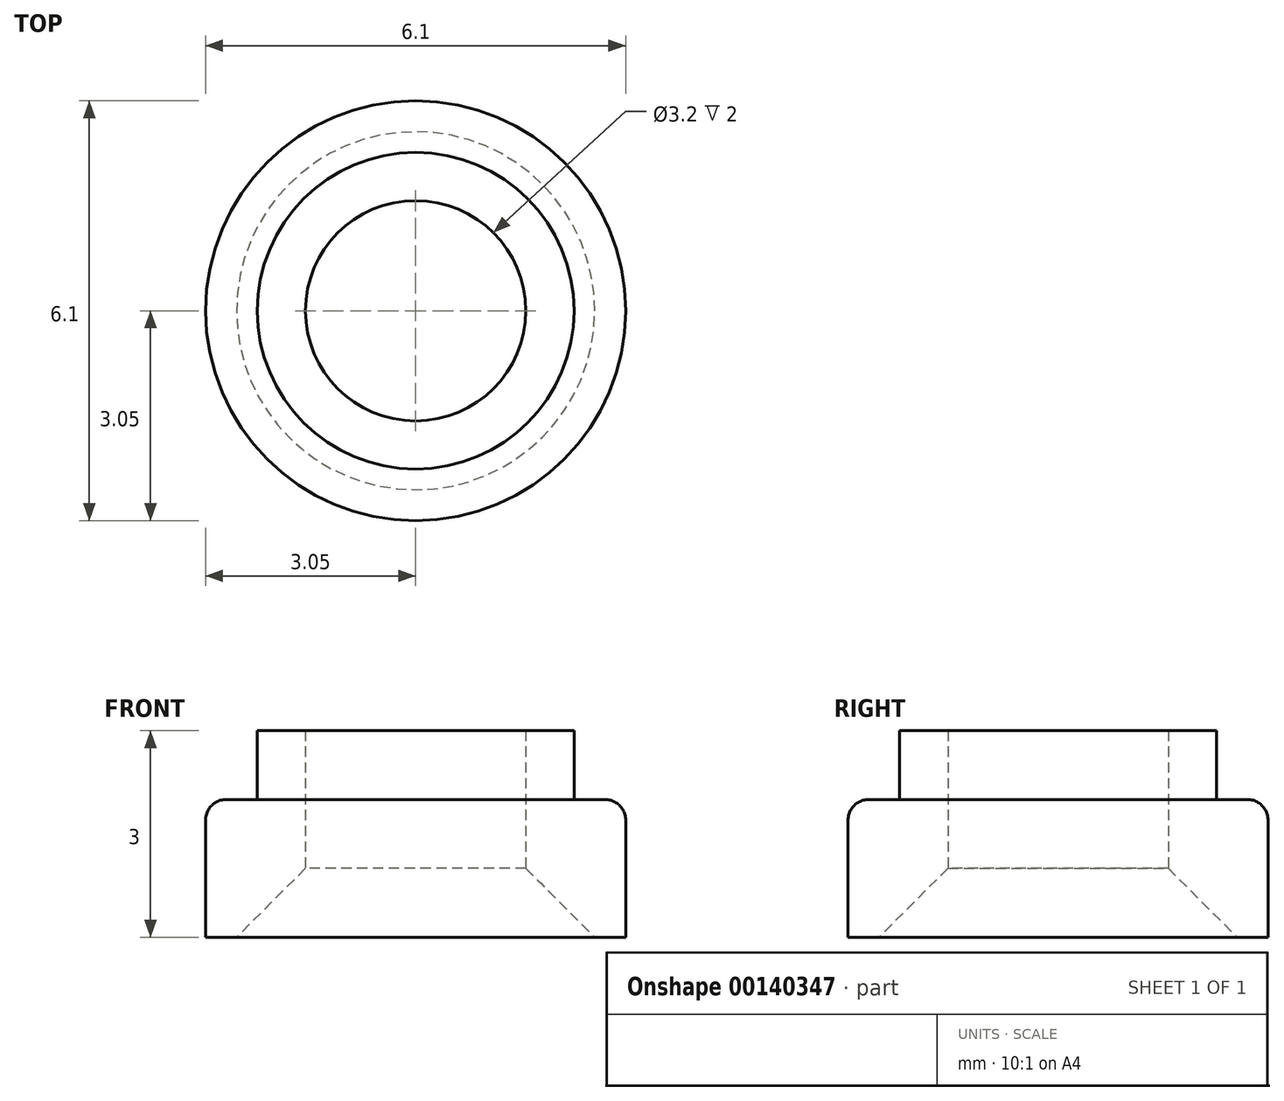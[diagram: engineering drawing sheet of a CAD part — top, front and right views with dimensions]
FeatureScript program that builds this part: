
annotation { "Feature Type Name" : "Feature", "Feature Type Description" : "" }
export const myFeature = defineFeature(function(context is Context, id is Id, definition is map)
    precondition{}
    {
        {
            var Q0;
            Q0=qCreatedBy(makeId("Top.planeOp"),FACE);
            var sketch = newSketch(context, id + "F0", { "sketchPlane" : qUnion([Q0])});
            skCircle(sketch, "E0", {"center": v(0, 0) * mm, "radius": 2.3 * mm});
            skCircle(sketch, "E1", {"center": v(0, 0) * mm, "radius": 3.05 * mm});
            skCircle(sketch, "E2", {"center": v(0, 0) * mm, "radius": 1.6 * mm});
            skSolve(sketch);
        }
        {
            var Q0;
            Q0=makeQuery(id+"F0.imprint","IMPRINT",FACE,{"disambiguationData":[TD([[makeQuery(id+"F0.imprint","IMPRINT",EDGE,{"derivedFrom":sQuery(id+"F0.wireOp",EDGE,"E0")}),1.0]])]});
            extrude(context, id + "F1", {"entities" : qUnion([Q0]), "depth" : 3 * mm});
        }
        {
            var Q0;
            Q0=makeQuery(id+"F0.imprint","IMPRINT",FACE,{"disambiguationData":[TD([[makeQuery(id+"F0.imprint","IMPRINT",EDGE,{"derivedFrom":sQuery(id+"F0.wireOp",EDGE,"E0")}),-1.0]])]});
            extrude(context, id + "F2", {"entities" : qUnion([Q0]), "operationType" : NewBodyOperationType.ADD, "depth" : 2 * mm});
        }
        {
            var Q0;
            Q0=makeQuery(id+"F2.opExtrude","CAP_EDGE",EDGE,{"disambiguationData":[OSD([sQuery(id+"F0.wireOp",EDGE,"E1")])],"isStart":false});
            fillet(context, id + "F3", {"entities" : qUnion([Q0]), "radius" : 0.3 * mm, "tangentPropagation" : true, "allowEdgeOverflow" : false});
        }
        {
            var Q0;
            Q0=makeQuery(id+"F1.opExtrude","CAP_EDGE",EDGE,{"disambiguationData":[OSD([sQuery(id+"F0.wireOp",EDGE,"E2")])],"isStart":true});
            chamfer(context, id + "F4", {"entities" : qUnion([Q0]), "width" : 1 * mm, "tangentPropagation" : true});
        }
    });
